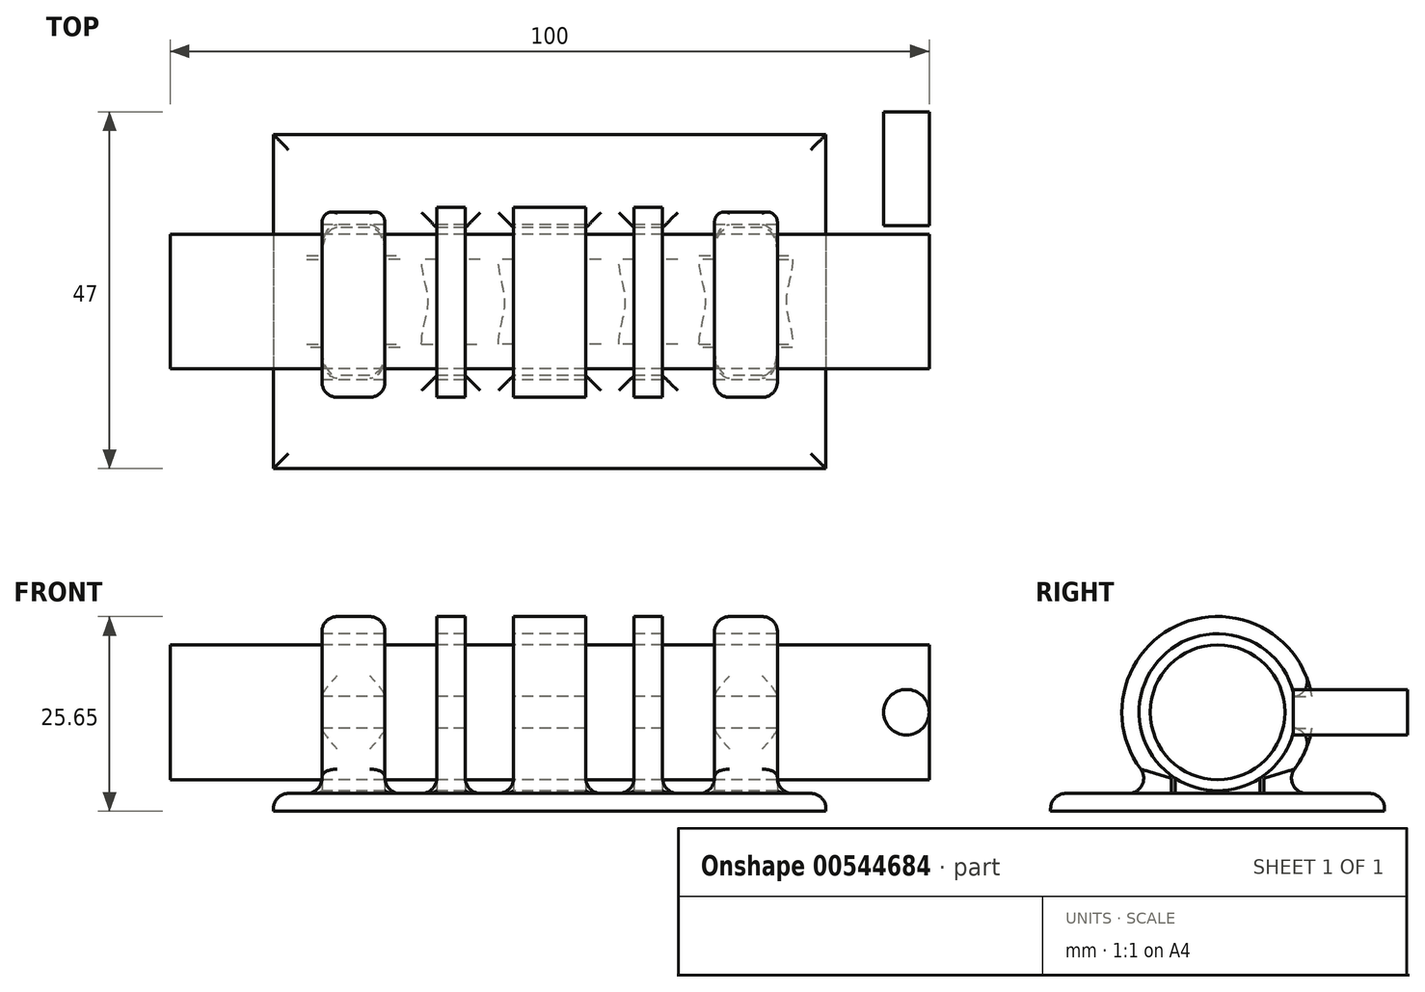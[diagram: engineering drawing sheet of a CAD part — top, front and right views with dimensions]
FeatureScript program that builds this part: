
annotation { "Feature Type Name" : "Feature", "Feature Type Description" : "" }
export const myFeature = defineFeature(function(context is Context, id is Id, definition is map)
    precondition{}
    {
        {
            var Q0;
            Q0=qCreatedBy(makeId("Right.planeOp"),FACE);
            var sketch = newSketch(context, id + "F0", { "sketchPlane" : qUnion([Q0])});
            skCircle(sketch, "E0", {"center": v(0, 0) * mm, "radius": 12.6 * mm});
            skCircle(sketch, "E1", {"center": v(0, 0) * mm, "radius": 10.34 * mm});
            skSolve(sketch);
        }
        {
            var Q0;
            Q0=makeQuery(id+"F0.imprint","IMPRINT",FACE,{"disambiguationData":[TD([[makeQuery(id+"F0.imprint","IMPRINT",EDGE,{"derivedFrom":sQuery(id+"F0.wireOp",EDGE,"E0")}),1.0]])]});
            extrude(context, id + "F1", {"entities" : qUnion([Q0]), "endBound" : BoundingType.SYMMETRIC, "depth" : 60 * mm, "offsetDistance" : 25 * mm});
        }
        {
            var Q0;
            Q0=qCreatedBy(makeId("Right.planeOp"),FACE);
            var sketch = newSketch(context, id + "F2", { "sketchPlane" : qUnion([Q0])});
            skLineSegment(sketch, "E2.bottom", {"start": v(0, -10.7) * mm, "end": v(22, -10.7) * mm});
            skLineSegment(sketch, "E2.top", {"start": v(0, -13.04) * mm, "end": v(22, -13.04) * mm});
            skLineSegment(sketch, "E2.left", {"start": v(0, -10.7) * mm, "end": v(0, -13.04) * mm});
            skLineSegment(sketch, "E2.right", {"start": v(22, -10.7) * mm, "end": v(22, -13.04) * mm});
            skLineSegment(sketch, "E3.MirrorCS", {"start": v(-22, -10.7) * mm, "end": v(-22, -13.04) * mm});
            skLineSegment(sketch, "E4.MirrorCS", {"start": v(0, -10.7) * mm, "end": v(-22, -10.7) * mm});
            skLineSegment(sketch, "E5.MirrorCS", {"start": v(0, -13.04) * mm, "end": v(-22, -13.04) * mm});
            skSolve(sketch);
        }
        {
            var Q0;
            Q0=qCreatedBy(makeId("Front.planeOp"),FACE);
            var sketch = newSketch(context, id + "F3", { "sketchPlane" : qUnion([Q0])});
            skLineSegment(sketch, "E6.bottom", {"start": v(-21.7, 17.97) * mm, "end": v(-14.88, 17.97) * mm});
            skLineSegment(sketch, "E6.top", {"start": v(-21.7, -21.48) * mm, "end": v(-14.88, -21.48) * mm});
            skLineSegment(sketch, "E6.left", {"start": v(-21.7, 17.97) * mm, "end": v(-21.7, -21.48) * mm});
            skLineSegment(sketch, "E6.right", {"start": v(-14.88, 17.97) * mm, "end": v(-14.88, -21.48) * mm});
            skLineSegment(sketch, "E7.MirrorCS", {"start": v(21.7, -21.48) * mm, "end": v(14.88, -21.48) * mm});
            skLineSegment(sketch, "E8.MirrorCS", {"start": v(21.7, 17.97) * mm, "end": v(14.88, 17.97) * mm});
            skLineSegment(sketch, "E9.MirrorCS", {"start": v(14.88, 17.97) * mm, "end": v(14.88, -21.48) * mm});
            skLineSegment(sketch, "E10.MirrorCS", {"start": v(21.7, 17.97) * mm, "end": v(21.7, -21.48) * mm});
            skLineSegment(sketch, "E11.bottom", {"start": v(11.12, 17.97) * mm, "end": v(4.76, 17.97) * mm});
            skLineSegment(sketch, "E11.top", {"start": v(11.12, -21.48) * mm, "end": v(4.76, -21.48) * mm});
            skLineSegment(sketch, "E11.left", {"start": v(11.12, 17.97) * mm, "end": v(11.12, -21.48) * mm});
            skLineSegment(sketch, "E11.right", {"start": v(4.76, 17.97) * mm, "end": v(4.76, -21.48) * mm});
            skLineSegment(sketch, "E12.MirrorCS", {"start": v(-11.12, 17.97) * mm, "end": v(-11.12, -21.48) * mm});
            skLineSegment(sketch, "E13.MirrorCS", {"start": v(-11.12, -21.48) * mm, "end": v(-4.76, -21.48) * mm});
            skLineSegment(sketch, "E14.MirrorCS", {"start": v(-11.12, 17.97) * mm, "end": v(-4.76, 17.97) * mm});
            skLineSegment(sketch, "E15.MirrorCS", {"start": v(-4.76, 17.97) * mm, "end": v(-4.76, -21.48) * mm});
            skSolve(sketch);
        }
        {
            var Q0;
            Q0 = qSketchRegion(id + "F3", true);
            extrude(context, id + "F4", {"entities" : qUnion([Q0]), "operationType" : NewBodyOperationType.REMOVE, "endBound" : BoundingType.SYMMETRIC, "oppositeDirection" : true, "depth" : 40 * mm, "offsetDistance" : 25 * mm});
        }
        {
            var Q0;
            Q0=qCreatedBy(makeId("Front.planeOp"),FACE);
            var sketch = newSketch(context, id + "F5", { "sketchPlane" : qUnion([Q0])});
            skLineSegment(sketch, "E16.bottom", {"start": v(39.87, -2.08) * mm, "end": v(-39.87, -2.08) * mm});
            skLineSegment(sketch, "E16.top", {"start": v(39.87, 2.08) * mm, "end": v(-39.87, 2.08) * mm});
            skLineSegment(sketch, "E16.left", {"start": v(39.87, -2.08) * mm, "end": v(39.87, 2.08) * mm});
            skLineSegment(sketch, "E16.right", {"start": v(-39.87, -2.08) * mm, "end": v(-39.87, 2.08) * mm});
            skPoint(sketch, "E16.middle", {"position": v(0, 0) * mm});
            skSolve(sketch);
        }
        {
            var Q0;
            Q0 = qSketchRegion(id + "F5", true);
            extrude(context, id + "F6", {"entities" : qUnion([Q0]), "operationType" : NewBodyOperationType.REMOVE, "oppositeDirection" : true, "depth" : 25 * mm, "offsetDistance" : 25 * mm});
        }
        {
            var Q0;
            Q0=qCreatedBy(makeId("Right.planeOp"),FACE);
            var sketch = newSketch(context, id + "F7", { "sketchPlane" : qUnion([Q0])});
            skCircle(sketch, "E17", {"center": v(0, 0) * mm, "radius": 8.88 * mm});
            skSolve(sketch);
        }
        {
            var Q0;
            Q0 = qSketchRegion(id + "F7", true);
            extrude(context, id + "F8", {"entities" : qUnion([Q0]), "endBound" : BoundingType.SYMMETRIC, "depth" : 100 * mm, "offsetDistance" : 25 * mm});
        }
        {
            var Q0;
            Q0=qCreatedBy(makeId("Front.planeOp"),FACE);
            cPlane(context, id + "F9", {"entities" : qUnion([Q0]), "cplaneType" : CPlaneType.OFFSET, "offset" : 10 * mm, "oppositeDirection" : true, "width" : 150 * mm, "height" : 150 * mm});
        }
        {
            var Q0;
            Q0=qCreatedBy(id+"F9.planeOp",FACE);
            var sketch = newSketch(context, id + "F10", { "sketchPlane" : qUnion([Q0])});
            skCircle(sketch, "E18", {"center": v(47, 0) * mm, "radius": 3 * mm});
            skSolve(sketch);
        }
        {
            var Q0;
            Q0 = qSketchRegion(id + "F10", true);
            extrude(context, id + "F11", {"entities" : qUnion([Q0]), "operationType" : NewBodyOperationType.ADD, "oppositeDirection" : true, "depth" : 15 * mm, "offsetDistance" : 25 * mm});
        }
        {
            var Q0;
            Q0=makeQuery(id+"F2.imprint","IMPRINT",FACE,{"disambiguationData":[TD([[makeQuery(id+"F2.imprint","IMPRINT",EDGE,{"derivedFrom":sQuery(id+"F2.wireOp",EDGE,"E2.left")}),-1.0]])]});
            var Q1;
            Q1=makeQuery(id+"F2.imprint","IMPRINT",FACE,{"disambiguationData":[TD([[makeQuery(id+"F2.imprint","IMPRINT",EDGE,{"derivedFrom":sQuery(id+"F2.wireOp",EDGE,"E2.bottom")}),-1.0]])]});
            extrude(context, id + "F12", {"entities" : qUnion([Q0, Q1]), "operationType" : NewBodyOperationType.ADD, "endBound" : BoundingType.SYMMETRIC, "depth" : 72.8 * mm, "offsetDistance" : 25 * mm});
        }
        {
            var Q0;
            {var subQ0=sQuery(id+"F0.wireOp",EDGE,"E0");Q0=makeQuery(id+"F4.boolean.opBoolean","SPLIT",FACE,{"disambiguationData":[TD([makeQuery(id+"F4.opExtrude","SWEPT_FACE",FACE,{"disambiguationData":[OSD([sQuery(id+"F3.wireOp",EDGE,"E6.left")])]})])],"derivedFrom":makeQuery(id+"F1.opExtrude","SWEPT_FACE",FACE,{"disambiguationData":[OSD([subQ0])]})});}
            var Q1;
            Q1=makeQuery(id+"F12.boolean.opBoolean","INTERSECT",EDGE,{"disambiguationData":[OD(1.0)],"derivedFrom":[makeQuery(id+"F4.boolean.opBoolean","SPLIT",FACE,{"disambiguationData":[TD([makeQuery(id+"F4.opExtrude","SWEPT_FACE",FACE,{"disambiguationData":[OSD([sQuery(id+"F3.wireOp",EDGE,"E6.right")])]})])],"derivedFrom":makeQuery(id+"F1.opExtrude","SWEPT_FACE",FACE,{"disambiguationData":[OSD([sQuery(id+"F0.wireOp",EDGE,"E0")])]})}),makeQuery(id+"F12.opExtrude","SWEPT_FACE",FACE,{"disambiguationData":[OSD([sQuery(id+"F2.wireOp",EDGE,"E2.bottom"),sQuery(id+"F2.wireOp",EDGE,"E4.MirrorCS")])]})]});
            var Q2;
            {var subQ0=sQuery(id+"F0.wireOp",EDGE,"E0");Q2=makeQuery(id+"F4.boolean.opBoolean","SPLIT",FACE,{"disambiguationData":[TD([makeQuery(id+"F4.opExtrude","SWEPT_FACE",FACE,{"disambiguationData":[OSD([sQuery(id+"F3.wireOp",EDGE,"E10.MirrorCS")])]})])],"derivedFrom":makeQuery(id+"F1.opExtrude","SWEPT_FACE",FACE,{"disambiguationData":[OSD([subQ0])]})});}
            var Q3;
            Q3=makeQuery(id+"F12.opExtrude","SWEPT_FACE",FACE,{"disambiguationData":[OSD([sQuery(id+"F2.wireOp",EDGE,"E2.bottom"),sQuery(id+"F2.wireOp",EDGE,"E4.MirrorCS")])]});
            fillet(context, id + "F13", {"entities" : qUnion([Q0, Q1, Q2, Q3]), "radius" : 2 * mm, "tangentPropagation" : true, "allowEdgeOverflow" : false});
        }
    });
